# Revit family: C2000R
name_source: partatom
category: Mechanical Equipment
revit_build: Autodesk Revit 2015 (Build: 20140223_1515(x64)
units: mm (PartAtom-declared; Revit-internal decimal feet)

## types (3) — shared parameters
Air flow space = No
Boundary box = No
Center X = 805 mm
Center X1 = 790 mm
Center Y = 177 mm
Center Y1 = 151 mm
D = 140 mm  [stored 0.459318 ft]
Distance between water holes = 33 mm  [stored 0.108268 ft]
Drop rod hole 1 = 25 mm  [stored 0.082021 ft]
Drop rod hole 2 = 22 mm
Flange length = 1609 mm  [stored 5.27887 ft]
Flange width = 353 mm  [stored 1.15814 ft]
Noise output dB (A) @3m high = 56
Noise output dB (A) @3m low = 50
Noise output dB (A) @3m med = 54
Product URL = http://www.thermoscreens.com
URL = http://www.thermoscreens.com
Unit length = 1579 mm  [stored 5.18045 ft]
Unit width = 301 mm  [stored 0.987533 ft]
Water hole length side = 165 mm

## per-type parameters (varying)
| type | Boundary box workspace | Heat output (kW) | Loading (A) per phase | Max air volume (m3/h) | Max velocity (m/s) | Supply (50Hz) | Weight (kg) |
| C2000AR | 250 mm | - | 1.1 | 2380 | 9 | 230V~1P&N | 35 |
| C2000ER | 250 mm | 9/18 | 27.2 | 2380 | 9 | 400V~3P&N | 37 |
| C2000WR 82/71 | 500 mm  [stored 1.64042 ft] | 12 | 1.1 | 2240 | 8.5 | 230V~1P&N | 41 |

note: [stored X ft] marks values corroborated as IEEE doubles in the binary element streams (Revit-internal decimal feet)

## geometry (parser evidence)
native form markers: Sweep x2
no freeform markers — native parametric forms only
